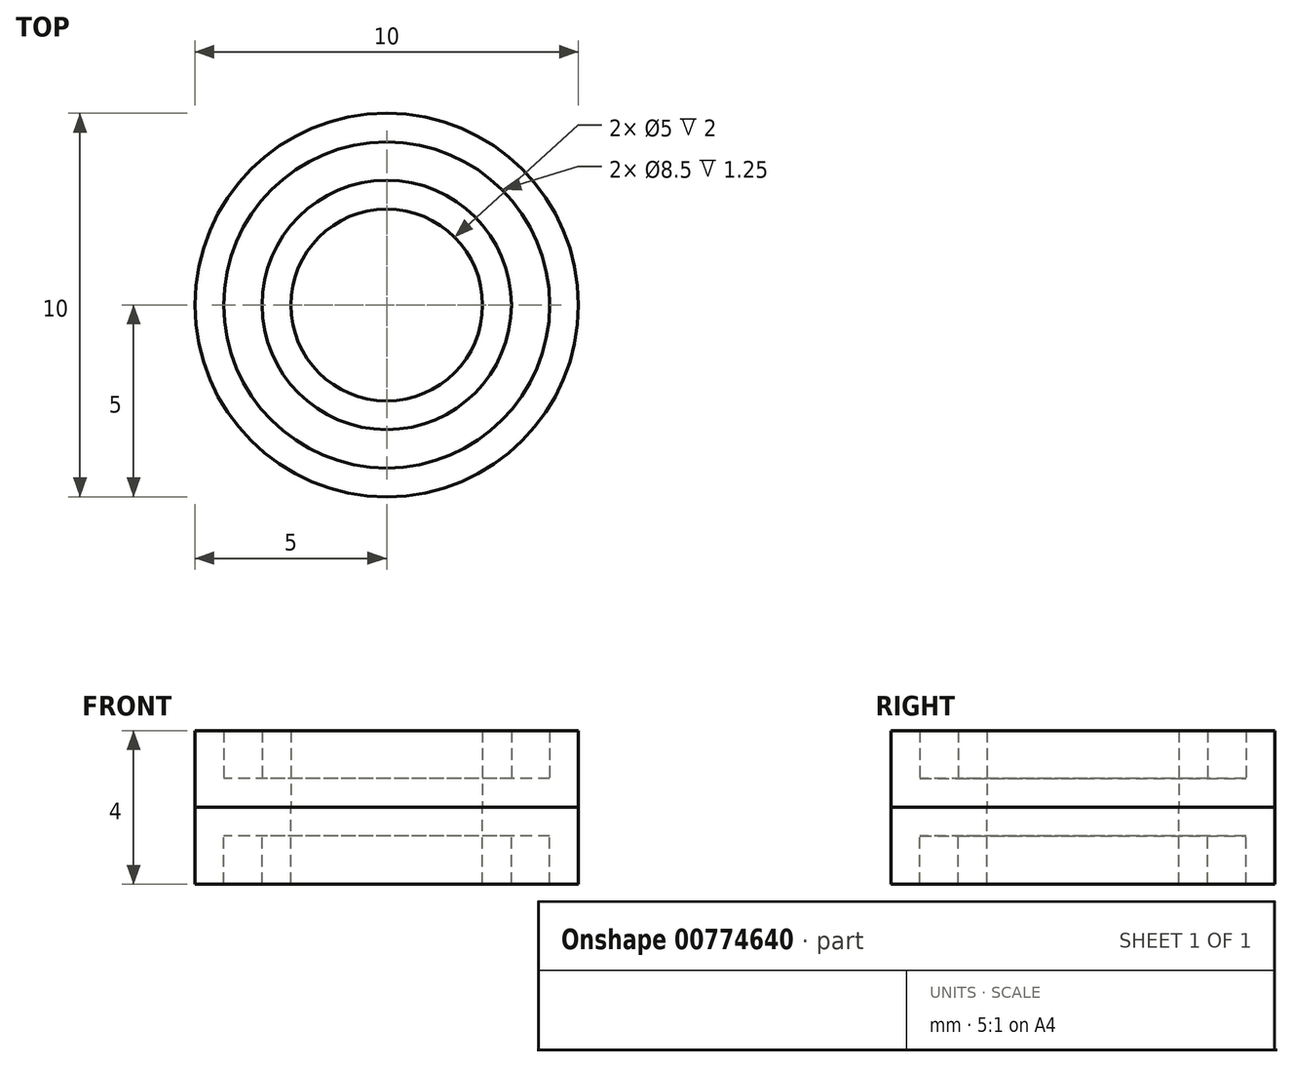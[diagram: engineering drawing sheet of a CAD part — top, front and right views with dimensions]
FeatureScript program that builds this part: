
annotation { "Feature Type Name" : "Feature", "Feature Type Description" : "" }
export const myFeature = defineFeature(function(context is Context, id is Id, definition is map)
    precondition{}
    {
        {
            var Q0;
            Q0=qCreatedBy(makeId("Top.planeOp"),FACE);
            var sketch = newSketch(context, id + "F0", { "sketchPlane" : qUnion([Q0])});
            skCircle(sketch, "E0", {"center": v(0, 0) * mm, "radius": 5 * mm});
            skCircle(sketch, "E1", {"center": v(0, 0) * mm, "radius": 2.5 * mm});
            skSolve(sketch);
        }
        {
            var Q0;
            Q0=makeQuery(id+"F0.imprint","IMPRINT",FACE,{"disambiguationData":[TD([[makeQuery(id+"F0.imprint","IMPRINT",EDGE,{"derivedFrom":sQuery(id+"F0.wireOp",EDGE,"E0")}),1.0]])]});
            extrude(context, id + "F1", {"entities" : qUnion([Q0]), "depth" : 2 * mm, "offsetDistance" : 25 * mm});
        }
        {
            var Q0;
            Q0=makeQuery(id+"F0.imprint","IMPRINT",FACE,{"disambiguationData":[TD([[makeQuery(id+"F0.imprint","IMPRINT",EDGE,{"derivedFrom":sQuery(id+"F0.wireOp",EDGE,"E0")}),1.0]])]});
            extrude(context, id + "F2", {"entities" : qUnion([Q0]), "oppositeDirection" : true, "depth" : 2 * mm, "offsetDistance" : 25 * mm});
        }
        {
            var Q0;
            Q0=makeQuery(id+"F1.opExtrude","CAP_FACE",FACE,{"disambiguationData":[OSD([sQuery(id+"F0.wireOp",EDGE,"E0"),sQuery(id+"F0.wireOp",EDGE,"E1")])],"isStart":false});
            var Q1;
            Q1=makeQuery(id+"F2.opExtrude","CAP_FACE",FACE,{"disambiguationData":[OSD([sQuery(id+"F0.wireOp",EDGE,"E0"),sQuery(id+"F0.wireOp",EDGE,"E1")])],"isStart":false});
            shell(context, id + "F3", {"entities" : qUnion([Q0, Q1]), "thickness" : (6 / 8) * mm});
        }
    });
